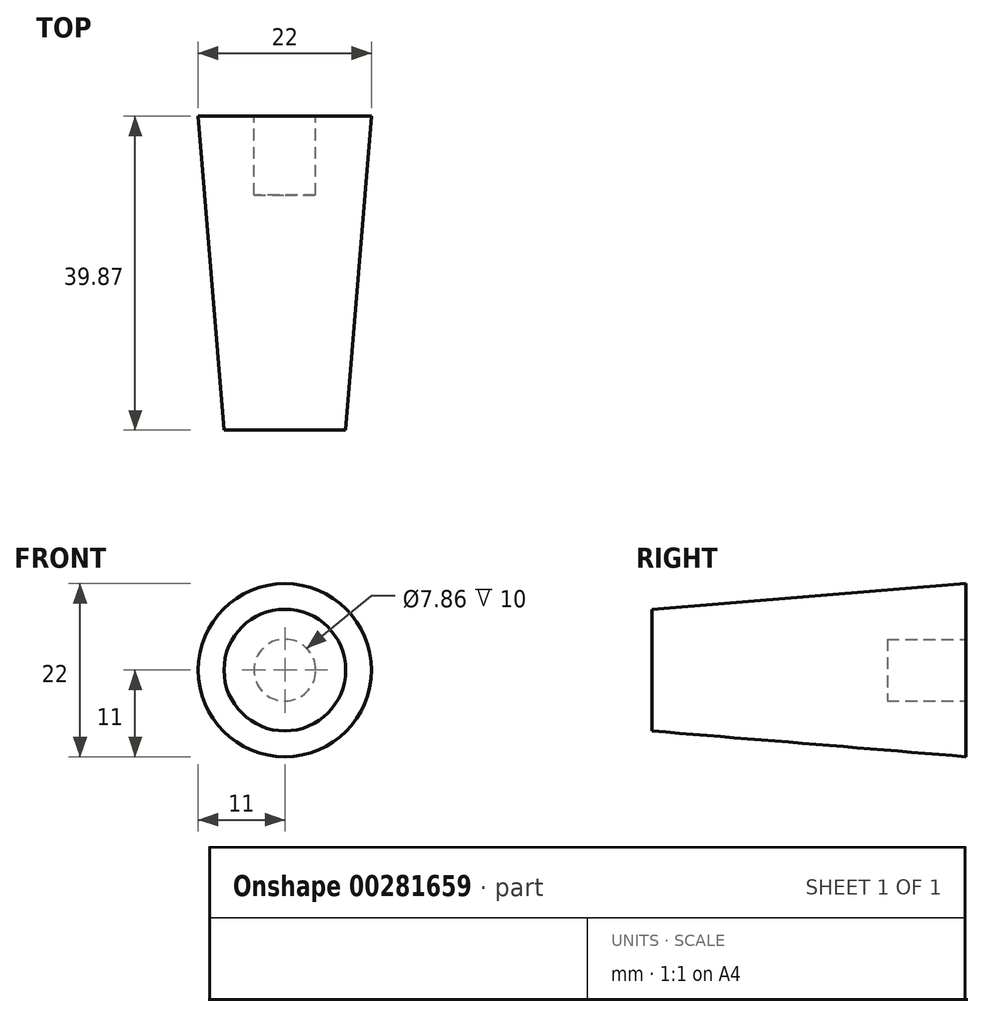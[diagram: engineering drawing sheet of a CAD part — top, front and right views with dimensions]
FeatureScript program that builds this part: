
annotation { "Feature Type Name" : "Feature", "Feature Type Description" : "" }
export const myFeature = defineFeature(function(context is Context, id is Id, definition is map)
    precondition{}
    {
        {
            var Q0;
            Q0=qCreatedBy(makeId("Top.planeOp"),FACE);
            var sketch = newSketch(context, id + "F0", { "sketchPlane" : qUnion([Q0])});
            skLineSegment(sketch, "E0", {"start": v(0, 0) * mm, "end": v(-11, 0) * mm});
            skLineSegment(sketch, "E1", {"start": v(-11, 0) * mm, "end": v(-7.73, -39.87) * mm});
            skLineSegment(sketch, "E2", {"start": v(-7.73, -39.87) * mm, "end": v(0, -39.87) * mm});
            skLineSegment(sketch, "E3", {"start": v(0, -39.87) * mm, "end": v(0, 0) * mm});
            skSolve(sketch);
        }
        {
            var Q0;
            Q0 = qSketchRegion(id + "F0", true);
            var Q1;
            Q1=sQuery(id+"F0.wireOp",EDGE,"E3");
            revolve(context, id + "F1", {"entities" : qUnion([Q0]), "axis" : qUnion([Q1]), "revolveType" : RevolveType.FULL});
        }
        {
            var Q0;
            Q0=makeQuery(id+"F1.opRevolve","SWEPT_FACE",FACE,{"disambiguationData":[OSD([sQuery(id+"F0.wireOp",EDGE,"E0")])]});
            var sketch = newSketch(context, id + "F2", { "sketchPlane" : qUnion([Q0])});
            skCircle(sketch, "E4", {"center": v(0, 0) * mm, "radius": 3.93 * mm});
            skSolve(sketch);
        }
        {
            var Q0;
            Q0=makeQuery(id+"F2.imprint","IMPRINT",FACE,{"disambiguationData":[TD([[makeQuery(id+"F2.imprint","IMPRINT",EDGE,{"derivedFrom":sQuery(id+"F2.wireOp",EDGE,"E4")}),1.0]])]});
            extrude(context, id + "F3", {"entities" : qUnion([Q0]), "operationType" : NewBodyOperationType.REMOVE, "oppositeDirection" : true, "depth" : 10 * mm});
        }
    });
